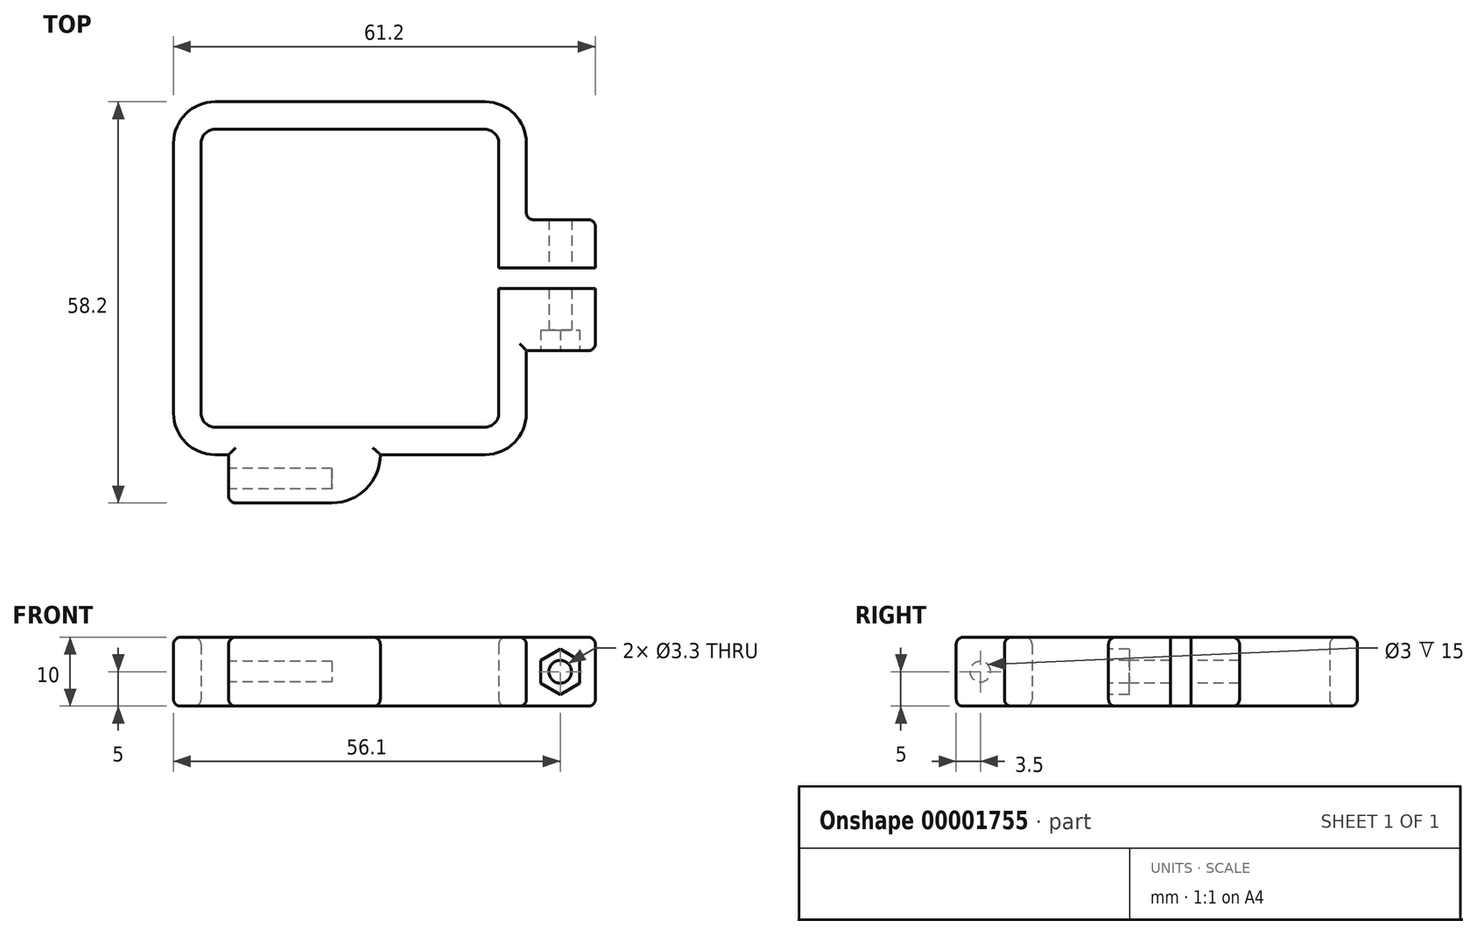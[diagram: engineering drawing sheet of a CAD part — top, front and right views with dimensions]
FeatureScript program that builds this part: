
annotation { "Feature Type Name" : "Feature", "Feature Type Description" : "" }
export const myFeature = defineFeature(function(context is Context, id is Id, definition is map)
    precondition{}
    {
        {
            var Q0;
            Q0=qCreatedBy(makeId("Top.planeOp"),FACE);
            var sketch = newSketch(context, id + "F0", { "sketchPlane" : qUnion([Q0])});
            skLineSegment(sketch, "E0.rect.bottom", {"start": v(19.6, 21.6) * mm, "end": v(-19.6, 21.6) * mm});
            skLineSegment(sketch, "E0.rect.top", {"start": v(19.6, -21.6) * mm, "end": v(-19.6, -21.6) * mm});
            skLineSegment(sketch, "E0.rect.left", {"start": v(21.6, 19.6) * mm, "end": v(21.6, -19.6) * mm});
            skLineSegment(sketch, "E0.rect.right", {"start": v(-21.6, 19.6) * mm, "end": v(-21.6, -19.6) * mm});
            skPoint(sketch, "E0.rect.middle", {"position": v(0, 0) * mm});
            skPoint(sketch, "E1.visualSharp", {"position": v(-21.6, 21.6) * mm});
            skArc(sketch, "E1.filletArc", {"start": v(-19.6, 21.6) * mm, "mid": v(-21.01, 21.01) * mm, "end": v(-21.6, 19.6) * mm});
            skPoint(sketch, "E2.visualSharp", {"position": v(-21.6, -21.6) * mm});
            skArc(sketch, "E2.filletArc", {"start": v(-21.6, -19.6) * mm, "mid": v(-21.01, -21.01) * mm, "end": v(-19.6, -21.6) * mm});
            skPoint(sketch, "E3.visualSharp", {"position": v(21.6, -21.6) * mm});
            skArc(sketch, "E3.filletArc", {"start": v(19.6, -21.6) * mm, "mid": v(21.01, -21.01) * mm, "end": v(21.6, -19.6) * mm});
            skPoint(sketch, "E4.visualSharp", {"position": v(21.6, 21.6) * mm});
            skArc(sketch, "E4.filletArc", {"start": v(21.6, 19.6) * mm, "mid": v(21.01, 21.01) * mm, "end": v(19.6, 21.6) * mm});
            skArc(sketch, "E5.0", {"start": v(25.6, 19.6) * mm, "mid": v(23.84, 23.84) * mm, "end": v(19.6, 25.6) * mm});
            skLineSegment(sketch, "E5.1", {"start": v(25.6, 19.6) * mm, "end": v(25.6, -19.6) * mm});
            skArc(sketch, "E5.2", {"start": v(19.6, -25.6) * mm, "mid": v(23.84, -23.84) * mm, "end": v(25.6, -19.6) * mm});
            skLineSegment(sketch, "E5.3", {"start": v(19.6, -25.6) * mm, "end": v(-19.6, -25.6) * mm});
            skArc(sketch, "E5.4", {"start": v(-25.6, -19.6) * mm, "mid": v(-23.84, -23.84) * mm, "end": v(-19.6, -25.6) * mm});
            skLineSegment(sketch, "E5.5", {"start": v(19.6, 25.6) * mm, "end": v(-19.6, 25.6) * mm});
            skLineSegment(sketch, "E5.6", {"start": v(-25.6, 19.6) * mm, "end": v(-25.6, -19.6) * mm});
            skArc(sketch, "E5.7", {"start": v(-19.6, 25.6) * mm, "mid": v(-23.84, 23.84) * mm, "end": v(-25.6, 19.6) * mm});
            skSolve(sketch);
        }
        {
            var Q0;
            Q0=makeQuery(id+"F0.imprint","IMPRINT",FACE,{"disambiguationData":[TD([[makeQuery(id+"F0.imprint","IMPRINT",EDGE,{"derivedFrom":sQuery(id+"F0.wireOp",EDGE,"E0.rect.bottom")}),-1.0]])]});
            extrude(context, id + "F1", {"entities" : qUnion([Q0]), "depth" : 10 * mm});
        }
        {
            var Q0;
            Q0=makeQuery(id+"F1.opExtrude","SWEPT_FACE",FACE,{"disambiguationData":[OSD([sQuery(id+"F0.wireOp",EDGE,"E5.1")])]});
            var sketch = newSketch(context, id + "F2", { "sketchPlane" : qUnion([Q0])});
            skLineSegment(sketch, "E6.0", {"start": v(-25.6, 10) * mm, "end": v(-25.6, 0) * mm});
            skLineSegment(sketch, "E7.bottom", {"start": v(-10.5, 10) * mm, "end": v(8.5, 10) * mm});
            skLineSegment(sketch, "E7.top", {"start": v(-10.5, 0) * mm, "end": v(8.5, 0) * mm});
            skLineSegment(sketch, "E7.left", {"start": v(-10.5, 10) * mm, "end": v(-10.5, 0) * mm});
            skLineSegment(sketch, "E7.right", {"start": v(8.5, 10) * mm, "end": v(8.5, 0) * mm});
            skLineSegment(sketch, "E8", {"start": v(0, 0) * mm, "end": v(0, 10) * mm, "construction": true});
            skSolve(sketch);
        }
        {
            var Q0;
            Q0=makeQuery(id+"F2.imprint","IMPRINT",FACE,{"disambiguationData":[TD([[makeQuery(id+"F2.imprint","IMPRINT",EDGE,{"derivedFrom":sQuery(id+"F2.wireOp",EDGE,"E7.bottom")}),1.0]])]});
            extrude(context, id + "F3", {"entities" : qUnion([Q0]), "operationType" : NewBodyOperationType.ADD, "depth" : 10 * mm});
        }
        {
            var Q0;
            Q0=makeQuery(id+"Fd9rqMYvTikBHwG_1.boolean.opBoolean","MERGE",FACE,{"derivedFrom":[makeQuery(id+"F3.opExtrude","SWEPT_FACE",FACE,{"disambiguationData":[OSD([sQuery(id+"F2.wireOp",EDGE,"E7.left")])]}),makeQuery(id+"Fd9rqMYvTikBHwG_1.opExtrude","CAP_FACE",FACE,{"disambiguationData":[OSD([sQuery(id+"FNTkvmrOSF5oYCk_1.wireOp",EDGE,"794d470a-5c50-4978-96f5-1c63277c95f8")])],"isStart":true})]});
            var sketch = newSketch(context, id + "F4", { "sketchPlane" : qUnion([Q0])});
            skCircle(sketch, "E9", {"center": v(30.5, 5) * mm, "radius": 1.65 * mm});
            skSolve(sketch);
        }
        {
            var Q0;
            Q0 = qSketchRegion(id + "F4", true);
            extrude(context, id + "F5", {"entities" : qUnion([Q0]), "operationType" : NewBodyOperationType.REMOVE, "endBound" : BoundingType.THROUGH_ALL, "oppositeDirection" : true, "depth" : 25 * mm});
        }
        {
            var Q0;
            Q0=makeQuery(id+"Fd9rqMYvTikBHwG_1.boolean.opBoolean","MERGE",FACE,{"derivedFrom":[makeQuery(id+"F3.opExtrude","SWEPT_FACE",FACE,{"disambiguationData":[OSD([sQuery(id+"F2.wireOp",EDGE,"E7.left")])]}),makeQuery(id+"Fd9rqMYvTikBHwG_1.opExtrude","CAP_FACE",FACE,{"disambiguationData":[OSD([sQuery(id+"FNTkvmrOSF5oYCk_1.wireOp",EDGE,"794d470a-5c50-4978-96f5-1c63277c95f8")])],"isStart":true})]});
            var sketch = newSketch(context, id + "F6", { "sketchPlane" : qUnion([Q0])});
            skCircle(sketch, "E10.0", {"center": v(30.5, 5) * mm, "radius": 1.65 * mm, "construction": true});
            skCircle(sketch, "E11.cCircle", {"center": v(30.5, 5) * mm, "radius": 2.85 * mm, "construction": true});
            skLineSegment(sketch, "E11.0", {"start": v(33.35, 6.65) * mm, "end": v(33.35, 3.35) * mm});
            skLineSegment(sketch, "E11.1", {"start": v(33.35, 3.35) * mm, "end": v(30.5, 1.7) * mm});
            skLineSegment(sketch, "E11.2", {"start": v(30.5, 1.7) * mm, "end": v(27.65, 3.35) * mm});
            skLineSegment(sketch, "E11.3", {"start": v(27.65, 3.35) * mm, "end": v(27.65, 6.65) * mm});
            skLineSegment(sketch, "E11.4", {"start": v(27.65, 6.65) * mm, "end": v(30.5, 8.3) * mm});
            skLineSegment(sketch, "E11.5", {"start": v(30.5, 8.3) * mm, "end": v(33.35, 6.65) * mm});
            skPoint(sketch, "E11.0.midPoint", {"position": v(33.35, 5) * mm});
            skLineSegment(sketch, "E12.0", {"start": v(25.6, 10) * mm, "end": v(25.6, 0) * mm, "construction": true});
            skSolve(sketch);
        }
        {
            var Q0;
            Q0=makeQuery(id+"F6.imprint","IMPRINT",FACE,{"disambiguationData":[TD([[makeQuery(id+"F6.imprint","IMPRINT",EDGE,{"derivedFrom":sQuery(id+"F6.wireOp",EDGE,"E11.0")}),-1.0]])]});
            extrude(context, id + "F7", {"entities" : qUnion([Q0]), "operationType" : NewBodyOperationType.REMOVE, "oppositeDirection" : true, "depth" : 3 * mm});
        }
        {
            var Q0;
            Q0=makeQuery(id+"F3.boolean.opBoolean","MERGE",FACE,{"derivedFrom":[makeQuery(id+"F1.opExtrude","CAP_FACE",FACE,{"disambiguationData":[OSD([sQuery(id+"F0.wireOp",EDGE,"E0.rect.bottom"),sQuery(id+"F0.wireOp",EDGE,"E0.rect.top"),sQuery(id+"F0.wireOp",EDGE,"E0.rect.left"),sQuery(id+"F0.wireOp",EDGE,"E0.rect.right"),sQuery(id+"F0.wireOp",EDGE,"E1.filletArc"),sQuery(id+"F0.wireOp",EDGE,"E2.filletArc"),sQuery(id+"F0.wireOp",EDGE,"E3.filletArc"),sQuery(id+"F0.wireOp",EDGE,"E4.filletArc"),sQuery(id+"F0.wireOp",EDGE,"E5.0"),sQuery(id+"F0.wireOp",EDGE,"E5.1"),sQuery(id+"F0.wireOp",EDGE,"E5.2"),sQuery(id+"F0.wireOp",EDGE,"E5.3"),sQuery(id+"F0.wireOp",EDGE,"E5.4"),sQuery(id+"F0.wireOp",EDGE,"E5.5"),sQuery(id+"F0.wireOp",EDGE,"E5.6"),sQuery(id+"F0.wireOp",EDGE,"E5.7")])],"isStart":false}),makeQuery(id+"F3.opExtrude","SWEPT_FACE",FACE,{"disambiguationData":[OSD([sQuery(id+"F2.wireOp",EDGE,"E7.bottom")])]})]});
            var sketch = newSketch(context, id + "F8", { "sketchPlane" : qUnion([Q0])});
            skLineSegment(sketch, "E13", {"start": v(35.6, 6.5) * mm, "end": v(35.6, -12.5) * mm, "construction": true});
            skLineSegment(sketch, "E14.0", {"start": v(35.6, 5.5) * mm, "end": v(35.6, -13.5) * mm});
            skLineSegment(sketch, "E15.bottom", {"start": v(0, 1.5) * mm, "end": v(35.6, 1.5) * mm});
            skLineSegment(sketch, "E15.top", {"start": v(0, -1.5) * mm, "end": v(35.6, -1.5) * mm});
            skLineSegment(sketch, "E15.left", {"start": v(0, 1.5) * mm, "end": v(0, -1.5) * mm});
            skLineSegment(sketch, "E15.right", {"start": v(35.6, 2.5) * mm, "end": v(35.6, -2.5) * mm});
            skSolve(sketch);
        }
        {
            var Q0;
            Q0=makeQuery(id+"F1.opExtrude","SWEPT_FACE",FACE,{"disambiguationData":[OSD([sQuery(id+"F0.wireOp",EDGE,"E5.6")])]});
            cPlane(context, id + "F9", {"entities" : qUnion([Q0]), "cplaneType" : CPlaneType.OFFSET, "offset" : 8 * mm, "oppositeDirection" : true, "width" : 150 * mm, "height" : 150 * mm});
        }
        {
            var Q0;
            Q0=qCreatedBy(id+"F9.planeOp",FACE);
            var sketch = newSketch(context, id + "F10", { "sketchPlane" : qUnion([Q0])});
            skLineSegment(sketch, "E16.0", {"start": v(25.6, 10) * mm, "end": v(25.6, 0) * mm});
            skPoint(sketch, "E17", {"position": v(25.6, 5) * mm});
            skLineSegment(sketch, "E18", {"start": v(25.6, 5) * mm, "end": v(29.1, 5) * mm, "construction": true});
            skCircle(sketch, "E19", {"center": v(29.1, 5) * mm, "radius": 1.5 * mm});
            skLineSegment(sketch, "E20", {"start": v(25.6, 10) * mm, "end": v(32.6, 10) * mm});
            skLineSegment(sketch, "E21", {"start": v(32.6, 10) * mm, "end": v(32.6, 0) * mm});
            skLineSegment(sketch, "E22", {"start": v(32.6, 0) * mm, "end": v(25.6, 0) * mm});
            skPoint(sketch, "E23", {"position": v(29.1, 0) * mm});
            skSolve(sketch);
        }
        {
            var Q0;
            Q0=makeQuery(id+"F10.imprint","IMPRINT",FACE,{"disambiguationData":[TD([[makeQuery(id+"F10.imprint","IMPRINT",EDGE,{"derivedFrom":sQuery(id+"F10.wireOp",EDGE,"E19")}),-1.0]])]});
            extrude(context, id + "F11", {"entities" : qUnion([Q0]), "operationType" : NewBodyOperationType.ADD, "oppositeDirection" : true, "depth" : 15 * mm});
        }
        {
            var Q0;
            Q0=makeQuery(id+"F11.boolean.opBoolean","MERGE",FACE,{"derivedFrom":[makeQuery(id+"F3.boolean.opBoolean","MERGE",FACE,{"derivedFrom":[makeQuery(id+"F1.opExtrude","CAP_FACE",FACE,{"disambiguationData":[OSD([sQuery(id+"F0.wireOp",EDGE,"E0.rect.bottom"),sQuery(id+"F0.wireOp",EDGE,"E0.rect.top"),sQuery(id+"F0.wireOp",EDGE,"E0.rect.left"),sQuery(id+"F0.wireOp",EDGE,"E0.rect.right"),sQuery(id+"F0.wireOp",EDGE,"E1.filletArc"),sQuery(id+"F0.wireOp",EDGE,"E2.filletArc"),sQuery(id+"F0.wireOp",EDGE,"E3.filletArc"),sQuery(id+"F0.wireOp",EDGE,"E4.filletArc"),sQuery(id+"F0.wireOp",EDGE,"E5.0"),sQuery(id+"F0.wireOp",EDGE,"E5.1"),sQuery(id+"F0.wireOp",EDGE,"E5.2"),sQuery(id+"F0.wireOp",EDGE,"E5.3"),sQuery(id+"F0.wireOp",EDGE,"E5.4"),sQuery(id+"F0.wireOp",EDGE,"E5.5"),sQuery(id+"F0.wireOp",EDGE,"E5.6"),sQuery(id+"F0.wireOp",EDGE,"E5.7")])],"isStart":false}),makeQuery(id+"F3.opExtrude","SWEPT_FACE",FACE,{"disambiguationData":[OSD([sQuery(id+"F2.wireOp",EDGE,"E7.bottom")])]})]}),makeQuery(id+"F11.opExtrude","SWEPT_FACE",FACE,{"disambiguationData":[OSD([sQuery(id+"F10.wireOp",EDGE,"E20")])]})]});
            var sketch = newSketch(context, id + "F12", { "sketchPlane" : qUnion([Q0])});
            skPoint(sketch, "E24.0", {"position": v(-2.6, -32.6) * mm});
            skPoint(sketch, "E25.0", {"position": v(-2.6, -25.6) * mm});
            skArc(sketch, "E26", {"start": v(-2.6, -32.6) * mm, "mid": v(2.35, -30.55) * mm, "end": v(4.4, -25.6) * mm});
            skLineSegment(sketch, "E27.0", {"start": v(19.6, -25.6) * mm, "end": v(-2.6, -25.6) * mm});
            skPoint(sketch, "E28", {"position": v(4.4, -25.6) * mm});
            skSolve(sketch);
        }
        {
            var Q0;
            {var subQ2=sQuery(id+"F12.wireOp",EDGE,"E26");Q0=makeQuery(id+"F12.imprint","IMPRINT",FACE,{"disambiguationData":[TD([[makeQuery(id+"F12.imprint","IMPRINT",EDGE,{"derivedFrom":subQ2}),1.0]])]});}
            var Q1;
            Q1=makeQuery(id+"F11.boolean.opBoolean","MERGE",FACE,{"derivedFrom":[makeQuery(id+"F3.boolean.opBoolean","MERGE",FACE,{"derivedFrom":[makeQuery(id+"F1.opExtrude","CAP_FACE",FACE,{"disambiguationData":[OSD([sQuery(id+"F0.wireOp",EDGE,"E0.rect.bottom"),sQuery(id+"F0.wireOp",EDGE,"E0.rect.top"),sQuery(id+"F0.wireOp",EDGE,"E0.rect.left"),sQuery(id+"F0.wireOp",EDGE,"E0.rect.right"),sQuery(id+"F0.wireOp",EDGE,"E1.filletArc"),sQuery(id+"F0.wireOp",EDGE,"E2.filletArc"),sQuery(id+"F0.wireOp",EDGE,"E3.filletArc"),sQuery(id+"F0.wireOp",EDGE,"E4.filletArc"),sQuery(id+"F0.wireOp",EDGE,"E5.0"),sQuery(id+"F0.wireOp",EDGE,"E5.1"),sQuery(id+"F0.wireOp",EDGE,"E5.2"),sQuery(id+"F0.wireOp",EDGE,"E5.3"),sQuery(id+"F0.wireOp",EDGE,"E5.4"),sQuery(id+"F0.wireOp",EDGE,"E5.5"),sQuery(id+"F0.wireOp",EDGE,"E5.6"),sQuery(id+"F0.wireOp",EDGE,"E5.7")])],"isStart":true}),makeQuery(id+"F3.opExtrude","SWEPT_FACE",FACE,{"disambiguationData":[OSD([sQuery(id+"F2.wireOp",EDGE,"E7.top")])]})]}),makeQuery(id+"F11.opExtrude","SWEPT_FACE",FACE,{"disambiguationData":[OSD([sQuery(id+"F10.wireOp",EDGE,"E22")])]})]});
            extrude(context, id + "F13", {"entities" : qUnion([Q0]), "operationType" : NewBodyOperationType.ADD, "endBound" : BoundingType.UP_TO_SURFACE, "oppositeDirection" : true, "endBoundEntityFace" : qUnion([Q1]), "depth" : 25 * mm});
        }
        {
            var Q0;
            {var subQ0=sQuery(id+"F0.wireOp",EDGE,"E5.3");var subQ2=sQuery(id+"F0.wireOp",EDGE,"E5.2");Q0=makeQuery(id+"F11.boolean.opBoolean","SPLIT",EDGE,{"disambiguationData":[TD([makeQuery(id+"F1.opExtrude","SWEPT_FACE",FACE,{"disambiguationData":[OSD([subQ2])]})])],"derivedFrom":makeQuery(id+"F1.opExtrude","CAP_EDGE",EDGE,{"disambiguationData":[OSD([subQ0])],"isStart":false})});}
            var Q1;
            Q1=makeQuery(id+"F1.opExtrude","CAP_EDGE",EDGE,{"disambiguationData":[OSD([sQuery(id+"F0.wireOp",EDGE,"E5.6")])],"isStart":false});
            var Q2;
            Q2=makeQuery(id+"F11.opExtrude","CAP_EDGE",EDGE,{"disambiguationData":[OSD([sQuery(id+"F10.wireOp",EDGE,"1077b709-969a-4867-ba1d-8ad1f3a549f7.rect.bottom")])],"isStart":false});
            var Q3;
            Q3=makeQuery(id+"F11.opExtrude","CAP_EDGE",EDGE,{"disambiguationData":[OSD([sQuery(id+"F10.wireOp",EDGE,"1077b709-969a-4867-ba1d-8ad1f3a549f7.rect.bottom")])],"isStart":true});
            var Q4;
            Q4=makeQuery(id+"F1.opExtrude","CAP_EDGE",EDGE,{"disambiguationData":[OSD([sQuery(id+"F0.wireOp",EDGE,"E0.rect.right")])],"isStart":false});
            var Q5;
            Q5=makeQuery(id+"F1.opExtrude","CAP_EDGE",EDGE,{"disambiguationData":[OSD([sQuery(id+"F0.wireOp",EDGE,"E0.rect.right")])],"isStart":true});
            var Q6;
            {var subQ0=sQuery(id+"F0.wireOp",EDGE,"E5.3");var subQ2=sQuery(id+"F0.wireOp",EDGE,"E5.2");Q6=makeQuery(id+"F11.boolean.opBoolean","SPLIT",EDGE,{"disambiguationData":[TD([makeQuery(id+"F1.opExtrude","SWEPT_FACE",FACE,{"disambiguationData":[OSD([subQ2])]})])],"derivedFrom":makeQuery(id+"F1.opExtrude","CAP_EDGE",EDGE,{"disambiguationData":[OSD([subQ0])],"isStart":true})});}
            var Q7;
            Q7=makeQuery(id+"F1.opExtrude","CAP_EDGE",EDGE,{"disambiguationData":[OSD([sQuery(id+"F0.wireOp",EDGE,"E5.4")])],"isStart":true});
            fillet(context, id + "F14", {"entities" : qUnion([Q0, Q1, Q2, Q3, Q4, Q5, Q6, Q7]), "radius" : 1 * mm, "tangentPropagation" : true, "allowEdgeOverflow" : false});
        }
        {
            var Q0;
            Q0=makeQuery(id+"F11.opExtrude","CAP_EDGE",EDGE,{"disambiguationData":[OSD([sQuery(id+"F10.wireOp",EDGE,"E20")])],"isStart":true});
            var Q1;
            Q1=makeQuery(id+"F11.opExtrude","SWEPT_EDGE",EDGE,{"disambiguationData":[OSD([sQuery(id+"F10.wireOp",EDGE,"E20"),sQuery(id+"F10.wireOp",EDGE,"E21")])]});
            var Q2;
            Q2=makeQuery(id+"F11.opExtrude","CAP_EDGE",EDGE,{"disambiguationData":[OSD([sQuery(id+"F10.wireOp",EDGE,"E22")])],"isStart":true});
            var Q3;
            Q3=makeQuery(id+"F11.opExtrude","SWEPT_EDGE",EDGE,{"disambiguationData":[OSD([sQuery(id+"F10.wireOp",EDGE,"E21"),sQuery(id+"F10.wireOp",EDGE,"E22")])]});
            fillet(context, id + "F15", {"entities" : qUnion([Q0, Q1, Q2, Q3]), "radius" : 1 * mm, "tangentPropagation" : true, "allowEdgeOverflow" : false});
        }
        {
            var Q0;
            Q0=makeQuery(id+"F11.opExtrude","CAP_EDGE",EDGE,{"disambiguationData":[OSD([sQuery(id+"F10.wireOp",EDGE,"E16.0")])],"isStart":true});
            var Q1;
            Q1=makeQuery(id+"F11.opExtrude","CAP_EDGE",EDGE,{"disambiguationData":[OSD([sQuery(id+"F10.wireOp",EDGE,"E21")])],"isStart":true});
            var Q2;
            Q2=makeQuery(id+"F13.opExtrude","SWEPT_EDGE",EDGE,{"disambiguationData":[OSD([sQuery(id+"F12.wireOp",EDGE,"E26"),sQuery(id+"F12.wireOp",EDGE,"E27.0")])]});
            var Q3;
            Q3=makeQuery(id+"F3.opExtrude","CAP_EDGE",EDGE,{"disambiguationData":[OSD([sQuery(id+"F2.wireOp",EDGE,"E7.left")])],"isStart":true});
            var Q4;
            Q4=makeQuery(id+"F3.opExtrude","CAP_EDGE",EDGE,{"disambiguationData":[OSD([sQuery(id+"F2.wireOp",EDGE,"E7.right")])],"isStart":true});
            fillet(context, id + "F16", {"entities" : qUnion([Q0, Q1, Q2, Q3, Q4]), "radius" : 1 * mm, "tangentPropagation" : true, "allowEdgeOverflow" : false});
        }
        {
            var Q0;
            Q0 = qSketchRegion(id + "F8", true);
            var Q1;
            {var subQ0=sQuery(id+"F10.wireOp",EDGE,"E22");var subQ1=sQuery(id+"F2.wireOp",EDGE,"E7.top");var subQ2=sQuery(id+"F0.wireOp",EDGE,"E5.7");var subQ3=sQuery(id+"F0.wireOp",EDGE,"E5.6");var subQ4=sQuery(id+"F0.wireOp",EDGE,"E5.5");var subQ5=sQuery(id+"F0.wireOp",EDGE,"E5.4");var subQ6=sQuery(id+"F0.wireOp",EDGE,"E5.3");var subQ7=sQuery(id+"F0.wireOp",EDGE,"E5.2");var subQ8=sQuery(id+"F0.wireOp",EDGE,"E5.1");var subQ9=sQuery(id+"F0.wireOp",EDGE,"E5.0");var subQ10=sQuery(id+"F0.wireOp",EDGE,"E4.filletArc");var subQ11=sQuery(id+"F0.wireOp",EDGE,"E3.filletArc");var subQ12=sQuery(id+"F0.wireOp",EDGE,"E2.filletArc");var subQ13=sQuery(id+"F0.wireOp",EDGE,"E1.filletArc");var subQ14=sQuery(id+"F0.wireOp",EDGE,"E0.rect.right");var subQ15=sQuery(id+"F0.wireOp",EDGE,"E0.rect.left");var subQ16=sQuery(id+"F0.wireOp",EDGE,"E0.rect.top");var subQ17=sQuery(id+"F0.wireOp",EDGE,"E0.rect.bottom");Q1=makeQuery(id+"F13.boolean.opBoolean","MERGE",FACE,{"derivedFrom":[makeQuery(id+"F11.boolean.opBoolean","MERGE",FACE,{"derivedFrom":[makeQuery(id+"F3.boolean.opBoolean","MERGE",FACE,{"derivedFrom":[makeQuery(id+"F1.opExtrude","CAP_FACE",FACE,{"disambiguationData":[OSD([subQ17,subQ16,subQ15,subQ14,subQ13,subQ12,subQ11,subQ10,subQ9,subQ8,subQ7,subQ6,subQ5,subQ4,subQ3,subQ2])],"isStart":true}),makeQuery(id+"F3.opExtrude","SWEPT_FACE",FACE,{"disambiguationData":[OSD([subQ1])]})]}),makeQuery(id+"F11.opExtrude","SWEPT_FACE",FACE,{"disambiguationData":[OSD([subQ0])]})]}),makeQuery(id+"F13.opExtrude","CAP_FACE",FACE,{"disambiguationData":[OSD([subQ17,subQ16,subQ15,subQ14,subQ13,subQ12,subQ11,subQ10,subQ9,subQ8,subQ7,subQ6,subQ5,subQ4,subQ3,subQ2,subQ1,subQ0])],"isStart":false})]});}
            extrude(context, id + "F17", {"entities" : qUnion([Q0]), "operationType" : NewBodyOperationType.REMOVE, "endBound" : BoundingType.UP_TO_SURFACE, "oppositeDirection" : true, "endBoundEntityFace" : qUnion([Q1]), "depth" : 25 * mm});
        }
        {
            var Q0;
            {var subQ0=sQuery(id+"F2.wireOp",EDGE,"E7.left");var subQ1=sQuery(id+"F2.wireOp",EDGE,"E7.bottom");Q0=makeQuery(id+"F17.boolean.opBoolean","SPLIT",EDGE,{"disambiguationData":[TD([makeQuery(id+"F3.opExtrude","SWEPT_FACE",FACE,{"disambiguationData":[OSD([subQ0])]})])],"derivedFrom":makeQuery(id+"F3.opExtrude","CAP_EDGE",EDGE,{"disambiguationData":[OSD([subQ1])],"isStart":false})});}
            var Q1;
            {var subQ0=sQuery(id+"F2.wireOp",EDGE,"E7.right");var subQ1=sQuery(id+"F2.wireOp",EDGE,"E7.bottom");Q1=makeQuery(id+"F17.boolean.opBoolean","SPLIT",EDGE,{"disambiguationData":[TD([makeQuery(id+"F3.opExtrude","SWEPT_FACE",FACE,{"disambiguationData":[OSD([subQ0])]})])],"derivedFrom":makeQuery(id+"F3.opExtrude","CAP_EDGE",EDGE,{"disambiguationData":[OSD([subQ1])],"isStart":false})});}
            var Q2;
            {var subQ0=sQuery(id+"F2.wireOp",EDGE,"E7.right");var subQ17=sQuery(id+"F2.wireOp",EDGE,"E7.top");Q2=makeQuery(id+"F17.boolean.opBoolean","SPLIT",EDGE,{"disambiguationData":[TD([makeQuery(id+"F3.opExtrude","SWEPT_FACE",FACE,{"disambiguationData":[OSD([subQ0])]})])],"derivedFrom":makeQuery(id+"F3.opExtrude","CAP_EDGE",EDGE,{"disambiguationData":[OSD([subQ17])],"isStart":false})});}
            var Q3;
            {var subQ0=sQuery(id+"F2.wireOp",EDGE,"E7.left");var subQ1=sQuery(id+"F2.wireOp",EDGE,"E7.top");Q3=makeQuery(id+"F17.boolean.opBoolean","SPLIT",EDGE,{"disambiguationData":[TD([makeQuery(id+"F3.opExtrude","SWEPT_FACE",FACE,{"disambiguationData":[OSD([subQ0])]})])],"derivedFrom":makeQuery(id+"F3.opExtrude","CAP_EDGE",EDGE,{"disambiguationData":[OSD([subQ1])],"isStart":false})});}
            var Q4;
            Q4=makeQuery(id+"F3.opExtrude","CAP_EDGE",EDGE,{"disambiguationData":[OSD([sQuery(id+"F2.wireOp",EDGE,"E7.left")])],"isStart":false});
            var Q5;
            Q5=makeQuery(id+"F3.opExtrude","CAP_EDGE",EDGE,{"disambiguationData":[OSD([sQuery(id+"F2.wireOp",EDGE,"E7.right")])],"isStart":false});
            var Q6;
            Q6=makeQuery(id+"F3.opExtrude","SWEPT_EDGE",EDGE,{"disambiguationData":[OSD([sQuery(id+"F0.wireOp",EDGE,"E5.1"),sQuery(id+"F2.wireOp",EDGE,"E7.bottom"),sQuery(id+"F2.wireOp",EDGE,"E7.left")])]});
            var Q7;
            Q7=makeQuery(id+"F3.opExtrude","SWEPT_EDGE",EDGE,{"disambiguationData":[OSD([sQuery(id+"F0.wireOp",EDGE,"E5.1"),sQuery(id+"F2.wireOp",EDGE,"E7.top"),sQuery(id+"F2.wireOp",EDGE,"E7.left")])]});
            var Q8;
            Q8=makeQuery(id+"F3.opExtrude","SWEPT_EDGE",EDGE,{"disambiguationData":[OSD([sQuery(id+"F0.wireOp",EDGE,"E5.1"),sQuery(id+"F2.wireOp",EDGE,"E7.bottom"),sQuery(id+"F2.wireOp",EDGE,"E7.right")])]});
            var Q9;
            Q9=makeQuery(id+"F3.opExtrude","SWEPT_EDGE",EDGE,{"disambiguationData":[OSD([sQuery(id+"F0.wireOp",EDGE,"E5.1"),sQuery(id+"F2.wireOp",EDGE,"E7.top"),sQuery(id+"F2.wireOp",EDGE,"E7.right")])]});
            fillet(context, id + "F18", {"entities" : qUnion([Q0, Q1, Q2, Q3, Q4, Q5, Q6, Q7, Q8, Q9]), "radius" : 1 * mm, "tangentPropagation" : true, "allowEdgeOverflow" : false});
        }
    });
